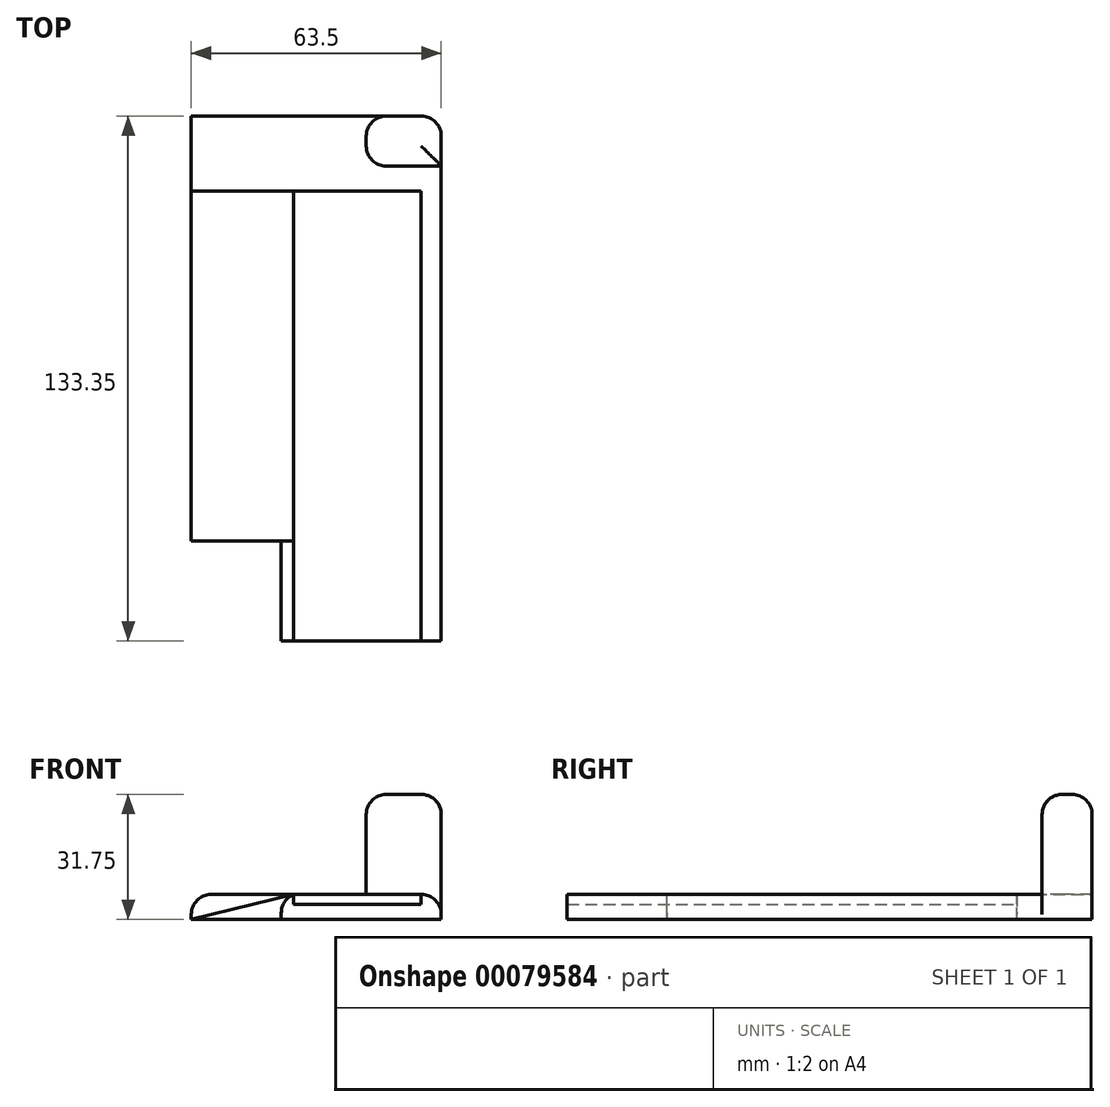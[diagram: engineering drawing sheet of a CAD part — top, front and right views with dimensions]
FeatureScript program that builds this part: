
annotation { "Feature Type Name" : "Feature", "Feature Type Description" : "" }
export const myFeature = defineFeature(function(context is Context, id is Id, definition is map)
    precondition{}
    {
        {
            var Q0;
            Q0=qCreatedBy(makeId("Top.planeOp"),FACE);
            var sketch = newSketch(context, id + "F0", { "sketchPlane" : qUnion([Q0])});
            skLineSegment(sketch, "E0.bottom", {"start": v(0, 0) * mm, "end": v(63.5, 0) * mm});
            skLineSegment(sketch, "E0.top", {"start": v(0, 133.35) * mm, "end": v(63.5, 133.35) * mm});
            skLineSegment(sketch, "E0.left", {"start": v(0, 0) * mm, "end": v(0, 133.35) * mm});
            skLineSegment(sketch, "E0.right", {"start": v(63.5, 0) * mm, "end": v(63.5, 133.35) * mm});
            skSolve(sketch);
        }
        {
            var Q0;
            Q0=makeQuery(id+"F0.imprint","IMPRINT",FACE,{"disambiguationData":[TD([[makeQuery(id+"F0.imprint","IMPRINT",EDGE,{"derivedFrom":sQuery(id+"F0.wireOp",EDGE,"E0.bottom")}),1.0]])]});
            extrude(context, id + "F1", {"entities" : qUnion([Q0]), "depth" : 6.35 * mm, "offsetDistance" : 25.4 * mm});
        }
        {
            var Q0;
            Q0=makeQuery(id+"F1.opExtrude","CAP_FACE",FACE,{"disambiguationData":[OSD([sQuery(id+"F0.wireOp",EDGE,"E0.bottom"),sQuery(id+"F0.wireOp",EDGE,"E0.top"),sQuery(id+"F0.wireOp",EDGE,"E0.left"),sQuery(id+"F0.wireOp",EDGE,"E0.right")])],"isStart":false});
            var sketch = newSketch(context, id + "F2", { "sketchPlane" : qUnion([Q0])});
            skLineSegment(sketch, "E1.bottom", {"start": v(44.45, 133.35) * mm, "end": v(63.5, 133.35) * mm});
            skLineSegment(sketch, "E1.top", {"start": v(44.45, 120.65) * mm, "end": v(63.5, 120.65) * mm});
            skLineSegment(sketch, "E1.left", {"start": v(44.45, 133.35) * mm, "end": v(44.45, 120.65) * mm});
            skLineSegment(sketch, "E1.right", {"start": v(63.5, 133.35) * mm, "end": v(63.5, 120.65) * mm});
            skSolve(sketch);
        }
        {
            var Q0;
            Q0=makeQuery(id+"F2.imprint","IMPRINT",FACE,{"disambiguationData":[TD([[makeQuery(id+"F2.imprint","IMPRINT",EDGE,{"derivedFrom":sQuery(id+"F2.wireOp",EDGE,"E1.bottom")}),-1.0]])]});
            extrude(context, id + "F3", {"entities" : qUnion([Q0]), "operationType" : NewBodyOperationType.ADD, "depth" : 25.4 * mm, "offsetDistance" : 25.4 * mm});
        }
        {
            var Q0;
            Q0=makeQuery(id+"F1.opExtrude","CAP_FACE",FACE,{"disambiguationData":[OSD([sQuery(id+"F0.wireOp",EDGE,"E0.bottom"),sQuery(id+"F0.wireOp",EDGE,"E0.top"),sQuery(id+"F0.wireOp",EDGE,"E0.left"),sQuery(id+"F0.wireOp",EDGE,"E0.right")])],"isStart":false});
            var sketch = newSketch(context, id + "F4", { "sketchPlane" : qUnion([Q0])});
            skLineSegment(sketch, "E2.bottom", {"start": v(26.04, 0) * mm, "end": v(58.42, 0) * mm});
            skLineSegment(sketch, "E2.top", {"start": v(26.03, 114.3) * mm, "end": v(58.42, 114.3) * mm});
            skLineSegment(sketch, "E2.left", {"start": v(26.04, 0) * mm, "end": v(26.03, 114.3) * mm});
            skLineSegment(sketch, "E2.right", {"start": v(58.42, 0) * mm, "end": v(58.42, 114.3) * mm});
            skSolve(sketch);
        }
        {
            var Q0;
            Q0=makeQuery(id+"F4.imprint","IMPRINT",FACE,{"disambiguationData":[TD([[makeQuery(id+"F4.imprint","IMPRINT",EDGE,{"derivedFrom":sQuery(id+"F4.wireOp",EDGE,"E2.bottom")}),1.0]])]});
            extrude(context, id + "F5", {"entities" : qUnion([Q0]), "operationType" : NewBodyOperationType.REMOVE, "oppositeDirection" : true, "depth" : 2.54 * mm, "offsetDistance" : 25.4 * mm});
        }
        {
            var Q0;
            Q0=makeQuery(id+"F1.opExtrude","SWEPT_FACE",FACE,{"disambiguationData":[OSD([sQuery(id+"F0.wireOp",EDGE,"E0.bottom")])]});
            var sketch = newSketch(context, id + "F6", { "sketchPlane" : qUnion([Q0])});
            skLineSegment(sketch, "E3", {"start": v(0, 0) * mm, "end": v(26.04, 6.35) * mm});
            skLineSegment(sketch, "E4", {"start": v(26.04, 6.35) * mm, "end": v(26.04, 13.33) * mm});
            skLineSegment(sketch, "E5", {"start": v(26.04, 13.33) * mm, "end": v(-1.22, 13.33) * mm});
            skLineSegment(sketch, "E6", {"start": v(-1.22, 13.33) * mm, "end": v(-1.22, 0) * mm});
            skLineSegment(sketch, "E7", {"start": v(-1.22, 0) * mm, "end": v(0, 0) * mm});
            skSolve(sketch);
        }
        {
            var Q0;
            Q0=makeQuery(id+"F6.imprint","IMPRINT",FACE,{"disambiguationData":[TD([[makeQuery(id+"F6.imprint","IMPRINT",EDGE,{"derivedFrom":sQuery(id+"F6.wireOp",EDGE,"E4")}),1.0]])]});
            var Q1;
            Q1=makeQuery(id+"F6.imprint","IMPRINT",FACE,{"disambiguationData":[TD([[makeQuery(id+"F6.imprint","IMPRINT",EDGE,{"derivedFrom":sQuery(id+"F6.wireOp",EDGE,"E3")}),1.0]])]});
            extrude(context, id + "F7", {"entities" : qUnion([Q0, Q1]), "operationType" : NewBodyOperationType.REMOVE, "oppositeDirection" : true, "depth" : 114.3 * mm, "offsetDistance" : 25.4 * mm});
        }
        {
            var Q0;
            Q0=makeQuery(id+"F1.opExtrude","CAP_FACE",FACE,{"disambiguationData":[OSD([sQuery(id+"F0.wireOp",EDGE,"E0.bottom"),sQuery(id+"F0.wireOp",EDGE,"E0.top"),sQuery(id+"F0.wireOp",EDGE,"E0.left"),sQuery(id+"F0.wireOp",EDGE,"E0.right")])],"isStart":true});
            var sketch = newSketch(context, id + "F8", { "sketchPlane" : qUnion([Q0])});
            skLineSegment(sketch, "E8.bottom", {"start": v(0, 0) * mm, "end": v(22.86, 0) * mm});
            skLineSegment(sketch, "E8.top", {"start": v(0, -25.4) * mm, "end": v(22.86, -25.4) * mm});
            skLineSegment(sketch, "E8.left", {"start": v(0, 0) * mm, "end": v(0, -25.4) * mm});
            skLineSegment(sketch, "E8.right", {"start": v(22.86, 0) * mm, "end": v(22.86, -25.4) * mm});
            skSolve(sketch);
        }
        {
            var Q0;
            Q0=makeQuery(id+"F8.imprint","IMPRINT",FACE,{"disambiguationData":[TD([[makeQuery(id+"F8.imprint","IMPRINT",EDGE,{"derivedFrom":sQuery(id+"F8.wireOp",EDGE,"E8.bottom")}),-1.0]])]});
            extrude(context, id + "F9", {"entities" : qUnion([Q0]), "operationType" : NewBodyOperationType.REMOVE, "endBound" : BoundingType.THROUGH_ALL, "oppositeDirection" : true, "depth" : 25.4 * mm, "offsetDistance" : 25.4 * mm});
        }
        {
            var Q0;
            Q0=makeQuery(id+"F1.opExtrude","CAP_EDGE",EDGE,{"disambiguationData":[OSD([sQuery(id+"F0.wireOp",EDGE,"E0.left")])],"isStart":false});
            var Q1;
            Q1=makeQuery(id+"F9.boolean.opBoolean","INTERSECT",EDGE,{"derivedFrom":[makeQuery(id+"F7.boolean.opBoolean","COPY",FACE,{"derivedFrom":makeQuery(id+"F7.opExtrude","SWEPT_FACE",FACE,{"disambiguationData":[OSD([sQuery(id+"F6.wireOp",EDGE,"E3")])]})}),makeQuery(id+"F9.opExtrude","SWEPT_FACE",FACE,{"disambiguationData":[OSD([sQuery(id+"F8.wireOp",EDGE,"E8.right")])]})]});
            var Q2;
            Q2=makeQuery(id+"F1.opExtrude","CAP_EDGE",EDGE,{"disambiguationData":[OSD([sQuery(id+"F0.wireOp",EDGE,"E0.right")])],"isStart":false});
            var Q3;
            Q3=makeQuery(id+"F3.opExtrude","SWEPT_EDGE",EDGE,{"disambiguationData":[OSD([sQuery(id+"F2.wireOp",EDGE,"E1.top"),sQuery(id+"F2.wireOp",EDGE,"E1.left")])]});
            var Q4;
            Q4=makeQuery(id+"F3.opExtrude","SWEPT_EDGE",EDGE,{"disambiguationData":[OSD([sQuery(id+"F0.wireOp",EDGE,"E0.top"),sQuery(id+"F2.wireOp",EDGE,"E1.bottom"),sQuery(id+"F2.wireOp",EDGE,"E1.left")])]});
            var Q5;
            Q5=makeQuery(id+"F3.opExtrude","CAP_EDGE",EDGE,{"disambiguationData":[OSD([sQuery(id+"F2.wireOp",EDGE,"E1.left")])],"isStart":true});
            var Q6;
            Q6=makeQuery(id+"F3.opExtrude","CAP_EDGE",EDGE,{"disambiguationData":[OSD([sQuery(id+"F2.wireOp",EDGE,"E1.top")])],"isStart":false});
            var Q7;
            Q7=makeQuery(id+"F3.opExtrude","CAP_EDGE",EDGE,{"disambiguationData":[OSD([sQuery(id+"F2.wireOp",EDGE,"E1.bottom")])],"isStart":false});
            var Q8;
            Q8=makeQuery(id+"F3.opExtrude","CAP_EDGE",EDGE,{"disambiguationData":[OSD([sQuery(id+"F2.wireOp",EDGE,"E1.right")])],"isStart":false});
            var Q9;
            Q9=makeQuery(id+"F3.opExtrude","CAP_EDGE",EDGE,{"disambiguationData":[OSD([sQuery(id+"F2.wireOp",EDGE,"E1.left")])],"isStart":false});
            var Q10;
            Q10=makeQuery(id+"F3.boolean.opBoolean","MERGE",EDGE,{"derivedFrom":[makeQuery(id+"F1.opExtrude","SWEPT_EDGE",EDGE,{"disambiguationData":[OSD([sQuery(id+"F0.wireOp",EDGE,"E0.top"),sQuery(id+"F0.wireOp",EDGE,"E0.right")])]}),makeQuery(id+"F3.opExtrude","SWEPT_EDGE",EDGE,{"disambiguationData":[OSD([sQuery(id+"F2.wireOp",EDGE,"E1.bottom"),sQuery(id+"F2.wireOp",EDGE,"E1.right")])]})]});
            fillet(context, id + "F10", {"entities" : qUnion([Q0, Q1, Q2, Q3, Q4, Q5, Q6, Q7, Q8, Q9, Q10]), "tangentPropagation" : true, "radius" : 5.08 * mm, "defaultsChanged" : false, "vertexSettings" : [], "allowEdgeOverflow" : false});
        }
    });
